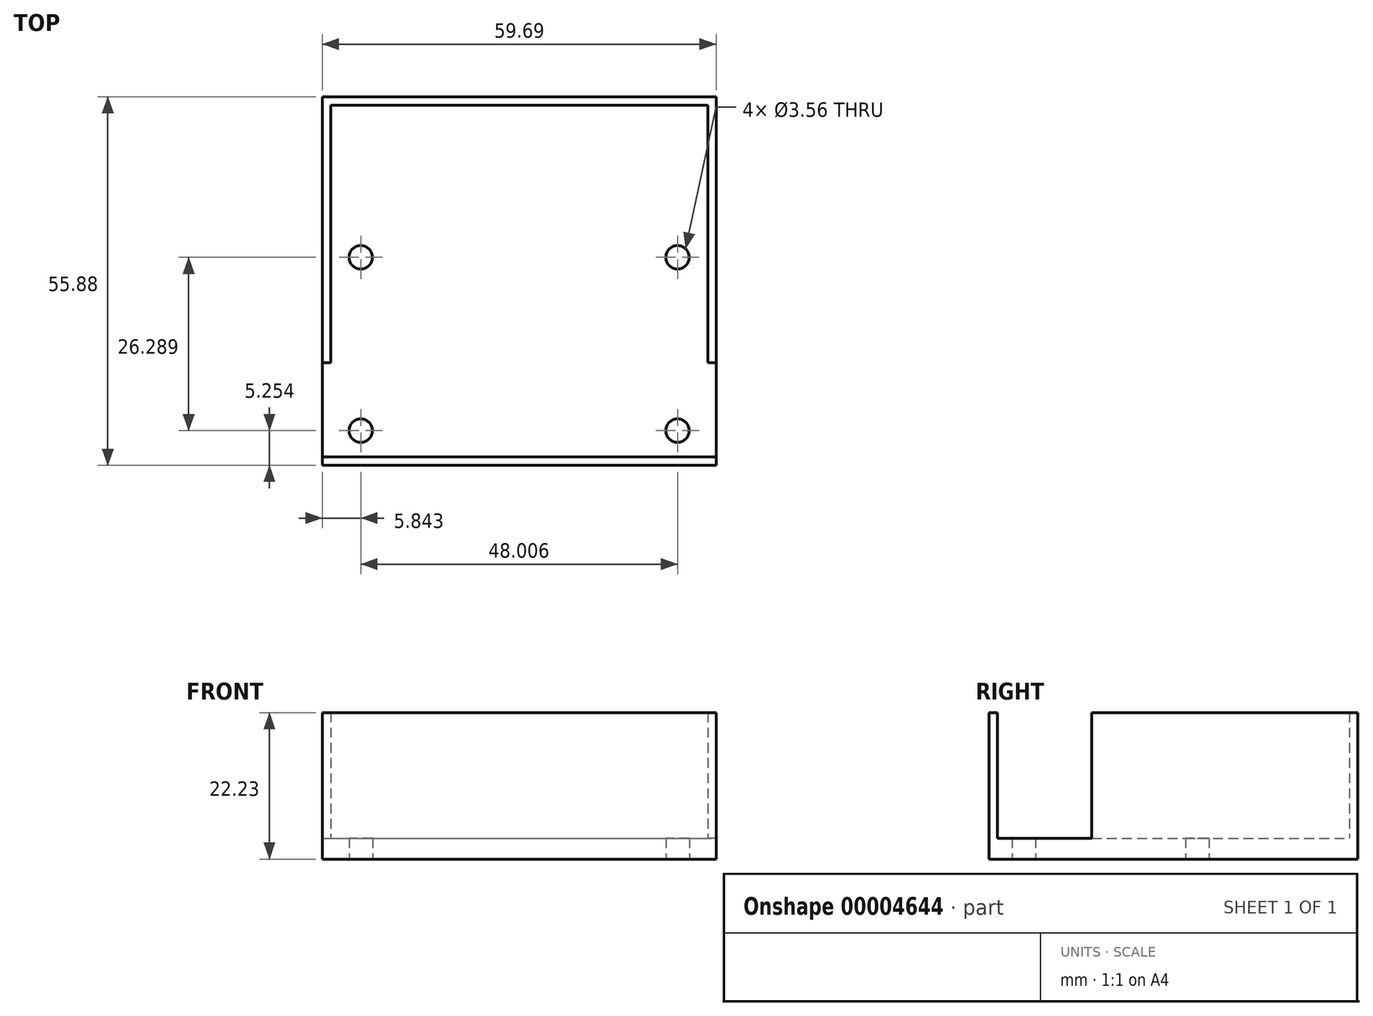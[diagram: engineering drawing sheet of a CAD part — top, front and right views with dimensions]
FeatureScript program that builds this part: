
annotation { "Feature Type Name" : "Feature", "Feature Type Description" : "" }
export const myFeature = defineFeature(function(context is Context, id is Id, definition is map)
    precondition{}
    {
        {
            var Q0;
            Q0=qCreatedBy(makeId("Top.planeOp"),FACE);
            var sketch = newSketch(context, id + "F0", { "sketchPlane" : qUnion([Q0])});
            skLineSegment(sketch, "E0", {"start": v(-20.33, -36.01) * mm, "end": v(36.82, -36.01) * mm});
            skLineSegment(sketch, "E1", {"start": v(-20.33, -36.01) * mm, "end": v(-20.33, 17.33) * mm});
            skLineSegment(sketch, "E2", {"start": v(-20.33, 17.33) * mm, "end": v(36.82, 17.33) * mm});
            skLineSegment(sketch, "E3", {"start": v(36.82, 17.33) * mm, "end": v(36.82, -36.01) * mm});
            skLineSegment(sketch, "E4", {"start": v(8.25, -36.01) * mm, "end": v(8.25, 54.35) * mm, "construction": true});
            skPoint(sketch, "E5", {"position": v(-15.76, -32.03) * mm});
            skCircle(sketch, "E6", {"center": v(-15.76, -32.03) * mm, "radius": 1.78 * mm});
            skCircle(sketch, "E7.0.MirrorC", {"center": v(32.25, -32.03) * mm, "radius": 1.78 * mm});
            skLineSegment(sketch, "E8.0", {"start": v(-21.6, -36.3) * mm, "end": v(-21.6, 17.04) * mm});
            skLineSegment(sketch, "E9.0.MirrorCS", {"start": v(38.1, -36.3) * mm, "end": v(38.1, 17.04) * mm});
            skLineSegment(sketch, "E10.0", {"start": v(-20.5, -37.28) * mm, "end": v(36.64, -37.28) * mm});
            skLineSegment(sketch, "E11", {"start": v(-20.5, -37.28) * mm, "end": v(-21.6, -37.28) * mm});
            skLineSegment(sketch, "E12", {"start": v(-21.6, -37.28) * mm, "end": v(-21.6, -36.3) * mm});
            skLineSegment(sketch, "E13", {"start": v(36.64, -37.28) * mm, "end": v(38.1, -37.28) * mm});
            skLineSegment(sketch, "E14", {"start": v(38.1, -37.28) * mm, "end": v(38.1, -36.3) * mm});
            skLineSegment(sketch, "E15.0.MirrorCS", {"start": v(-20.5, 18.6) * mm, "end": v(36.64, 18.6) * mm});
            skLineSegment(sketch, "E16", {"start": v(38.1, 17.04) * mm, "end": v(38.1, 18.6) * mm});
            skLineSegment(sketch, "E17", {"start": v(38.1, 18.6) * mm, "end": v(36.64, 18.6) * mm});
            skLineSegment(sketch, "E18", {"start": v(-21.6, 17.04) * mm, "end": v(-21.6, 18.6) * mm});
            skLineSegment(sketch, "E19", {"start": v(-21.6, 18.6) * mm, "end": v(-20.5, 18.6) * mm});
            skLineSegment(sketch, "E20", {"start": v(-15.76, -32.03) * mm, "end": v(-15.76, -5.74) * mm, "construction": true});
            skPoint(sketch, "E21", {"position": v(-15.76, -5.74) * mm});
            skLineSegment(sketch, "E22", {"start": v(-15.76, -18.88) * mm, "end": v(44, -18.88) * mm, "construction": true});
            skCircle(sketch, "E23.0.MirrorC", {"center": v(-15.76, -5.74) * mm, "radius": 1.78 * mm});
            skCircle(sketch, "E24.0.MirrorC", {"center": v(32.25, -5.74) * mm, "radius": 1.78 * mm});
            skLineSegment(sketch, "E25", {"start": v(-21.6, -21.72) * mm, "end": v(-20.33, -21.72) * mm});
            skLineSegment(sketch, "E26.0.MirrorCS", {"start": v(38.1, -21.72) * mm, "end": v(36.82, -21.72) * mm});
            skPoint(sketch, "E27.start.orphan", {"position": v(36.82, -3.11) * mm});
            skPoint(sketch, "E28.end.orphan", {"position": v(-20.33, -3.11) * mm});
            skPoint(sketch, "E29.end.orphan", {"position": v(-20.33, 18.6) * mm});
            skPoint(sketch, "E30.end.orphan", {"position": v(-20.33, -37.28) * mm});
            skLineSegment(sketch, "E31", {"start": v(-20.33, -36.01) * mm, "end": v(-21.6, -36.01) * mm});
            skLineSegment(sketch, "E32", {"start": v(36.82, -36.01) * mm, "end": v(38.1, -36.01) * mm});
            skPoint(sketch, "E33.0.MirrorCS.end.orphan", {"position": v(36.82, -37.28) * mm});
            skSolve(sketch);
        }
        {
            var Q0;
            {var subQ2=sQuery(id+"F0.wireOp",EDGE,"E0");Q0=makeQuery(id+"F0.imprint","IMPRINT",FACE,{"disambiguationData":[TD([[makeQuery(id+"F0.imprint","IMPRINT",EDGE,{"derivedFrom":subQ2}),1.0]])]});}
            extrude(context, id + "F1", {"entities" : qUnion([Q0]), "depth" : 3.17 * mm});
        }
        {
            var Q0;
            Q0=makeQuery(id+"F0.imprint","IMPRINT",FACE,{"disambiguationData":[TD([[makeQuery(id+"F0.imprint","IMPRINT",EDGE,{"derivedFrom":sQuery(id+"F0.wireOp",EDGE,"E0")}),-1.0]])]});
            extrude(context, id + "F2", {"entities" : qUnion([Q0]), "operationType" : NewBodyOperationType.ADD, "depth" : 22.22 * mm});
        }
        {
            var Q0;
            {var subQ7=sQuery(id+"F0.wireOp",EDGE,"E2");Q0=makeQuery(id+"F0.imprint","IMPRINT",FACE,{"disambiguationData":[TD([[makeQuery(id+"F0.imprint","IMPRINT",EDGE,{"derivedFrom":subQ7}),1.0]])]});}
            extrude(context, id + "F3", {"entities" : qUnion([Q0]), "operationType" : NewBodyOperationType.ADD, "depth" : 22.22 * mm});
        }
        {
            var Q0;
            {var subQ2=sQuery(id+"F0.wireOp",EDGE,"E11");Q0=makeQuery(id+"F0.imprint","IMPRINT",FACE,{"disambiguationData":[TD([[makeQuery(id+"F0.imprint","IMPRINT",EDGE,{"derivedFrom":subQ2}),-1.0]])]});}
            extrude(context, id + "F4", {"entities" : qUnion([Q0]), "operationType" : NewBodyOperationType.ADD, "depth" : 3.17 * mm});
        }
        {
            var Q0;
            {var subQ2=sQuery(id+"F0.wireOp",EDGE,"E14");Q0=makeQuery(id+"F0.imprint","IMPRINT",FACE,{"disambiguationData":[TD([[makeQuery(id+"F0.imprint","IMPRINT",EDGE,{"derivedFrom":subQ2}),1.0]])]});}
            extrude(context, id + "F5", {"entities" : qUnion([Q0]), "operationType" : NewBodyOperationType.ADD, "depth" : 3.17 * mm});
        }
        {
            var Q0;
            {var subQ1=sQuery(id+"F0.wireOp",EDGE,"E25");Q0=makeQuery(id+"F0.imprint","IMPRINT",FACE,{"disambiguationData":[TD([[makeQuery(id+"F0.imprint","IMPRINT",EDGE,{"derivedFrom":subQ1}),-1.0]])]});}
            extrude(context, id + "F6", {"entities" : qUnion([Q0]), "operationType" : NewBodyOperationType.ADD, "depth" : 3.17 * mm});
        }
        {
            var Q0;
            {var subQ1=sQuery(id+"F0.wireOp",EDGE,"E26.0.MirrorCS");Q0=makeQuery(id+"F0.imprint","IMPRINT",FACE,{"disambiguationData":[TD([[makeQuery(id+"F0.imprint","IMPRINT",EDGE,{"derivedFrom":subQ1}),1.0]])]});}
            extrude(context, id + "F7", {"entities" : qUnion([Q0]), "operationType" : NewBodyOperationType.ADD, "depth" : 3.17 * mm});
        }
    });
